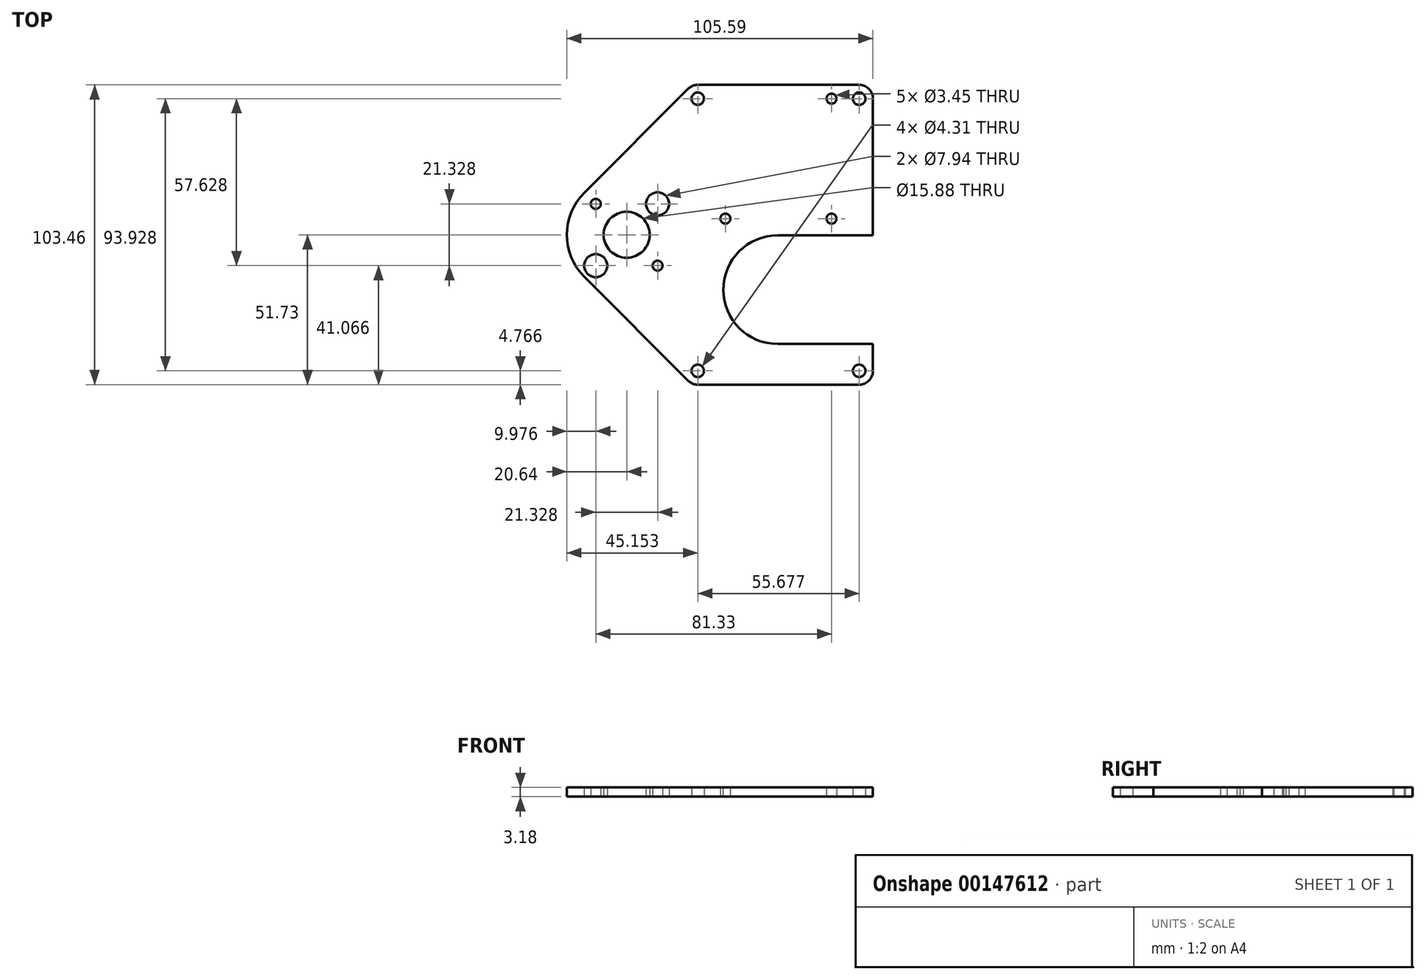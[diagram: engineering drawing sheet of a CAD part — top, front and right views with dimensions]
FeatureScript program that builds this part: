
annotation { "Feature Type Name" : "Feature", "Feature Type Description" : "" }
export const myFeature = defineFeature(function(context is Context, id is Id, definition is map)
    precondition{}
    {
        {
            var Q0;
            Q0=qCreatedBy(makeId("Top.planeOp"),FACE);
            var sketch = newSketch(context, id + "F0", { "sketchPlane" : qUnion([Q0])});
            skPoint(sketch, "E0.rect.middle", {"position": v(0, 0) * mm});
            skCircle(sketch, "E1", {"center": v(0, 0) * mm, "radius": 7.94 * mm});
            skLineSegment(sketch, "E2", {"start": v(0, 0) * mm, "end": v(84.95, 0) * mm, "construction": true});
            skLineSegment(sketch, "E3", {"start": v(84.95, 0) * mm, "end": v(84.95, 0) * mm});
            skLineSegment(sketch, "E4", {"start": v(-14.6, 14.6) * mm, "end": v(21.15, 50.33) * mm});
            skLineSegment(sketch, "E5", {"start": v(-14.6, -14.6) * mm, "end": v(21.15, -50.33) * mm});
            skCircle(sketch, "E6", {"center": v(24.51, 46.96) * mm, "radius": 2.15 * mm});
            skArc(sketch, "E7", {"start": v(24.51, 51.73) * mm, "mid": v(22.7, 51.36) * mm, "end": v(21.15, 50.33) * mm});
            skLineSegment(sketch, "E8", {"start": v(24.51, 51.73) * mm, "end": v(84.95, 51.73) * mm});
            skLineSegment(sketch, "E9", {"start": v(84.95, 51.73) * mm, "end": v(84.95, -51.73) * mm});
            skLineSegment(sketch, "E10", {"start": v(84.95, -51.73) * mm, "end": v(24.51, -51.73) * mm});
            skArc(sketch, "E11", {"start": v(21.15, -50.33) * mm, "mid": v(22.7, -51.36) * mm, "end": v(24.51, -51.73) * mm});
            skLineSegment(sketch, "E12", {"start": v(80.2, 46.96) * mm, "end": v(80.2, 51.73) * mm, "construction": true});
            skLineSegment(sketch, "E13", {"start": v(80.2, 46.96) * mm, "end": v(84.95, 46.96) * mm, "construction": true});
            skLineSegment(sketch, "E14", {"start": v(24.51, 46.96) * mm, "end": v(24.51, 51.73) * mm, "construction": true});
            skCircle(sketch, "E15", {"center": v(80.2, 46.96) * mm, "radius": 2.15 * mm});
            skCircle(sketch, "E16", {"center": v(80.2, -46.96) * mm, "radius": 2.15 * mm});
            skCircle(sketch, "E17", {"center": v(24.51, -46.96) * mm, "radius": 2.15 * mm});
            skArc(sketch, "E18", {"start": v(-14.6, 14.6) * mm, "mid": v(-20.64, 0) * mm, "end": v(-14.6, -14.6) * mm});
            skLineSegment(sketch, "E19", {"start": v(80.2, 46.96) * mm, "end": v(70.67, 46.96) * mm, "construction": true});
            skCircle(sketch, "E20", {"center": v(70.67, 46.96) * mm, "radius": 1.73 * mm});
            skLineSegment(sketch, "E21", {"start": v(24.51, -46.96) * mm, "end": v(80.2, -46.96) * mm, "construction": true});
            skLineSegment(sketch, "E22", {"start": v(70.67, 46.96) * mm, "end": v(70.67, 5.56) * mm, "construction": true});
            skCircle(sketch, "E23", {"center": v(70.67, 5.56) * mm, "radius": 1.73 * mm});
            skLineSegment(sketch, "E24", {"start": v(70.67, 46.96) * mm, "end": v(34.04, 46.96) * mm, "construction": true});
            skLineSegment(sketch, "E25", {"start": v(34.04, 46.96) * mm, "end": v(24.51, 46.96) * mm, "construction": true});
            skLineSegment(sketch, "E26", {"start": v(80.2, 46.96) * mm, "end": v(80.2, -46.96) * mm, "construction": true});
            skLineSegment(sketch, "E27", {"start": v(34.04, 46.96) * mm, "end": v(34.04, 5.56) * mm, "construction": true});
            skCircle(sketch, "E28", {"center": v(34.04, 5.56) * mm, "radius": 1.73 * mm});
            skLineSegment(sketch, "E29.bottom", {"start": v(10.66, -10.66) * mm, "end": v(-10.66, -10.66) * mm, "construction": true});
            skLineSegment(sketch, "E29.top", {"start": v(10.66, 10.66) * mm, "end": v(-10.66, 10.66) * mm, "construction": true});
            skLineSegment(sketch, "E29.left", {"start": v(10.66, -10.66) * mm, "end": v(10.66, 10.66) * mm, "construction": true});
            skLineSegment(sketch, "E29.right", {"start": v(-10.66, -10.66) * mm, "end": v(-10.66, 10.66) * mm, "construction": true});
            skCircle(sketch, "E30", {"center": v(-10.66, 10.66) * mm, "radius": 5.56 * mm, "construction": true});
            skCircle(sketch, "E31", {"center": v(0, 0) * mm, "radius": 9.53 * mm, "construction": true});
            skCircle(sketch, "E32", {"center": v(-10.66, 10.66) * mm, "radius": 1.73 * mm});
            skCircle(sketch, "E33", {"center": v(10.66, 10.66) * mm, "radius": 3.97 * mm});
            skCircle(sketch, "E34", {"center": v(10.66, -10.66) * mm, "radius": 1.73 * mm});
            skCircle(sketch, "E35", {"center": v(-10.66, -10.66) * mm, "radius": 3.97 * mm});
            skSolve(sketch);
        }
        {
            var Q0;
            Q0=qSketchRegion(id+"F0",true);
            extrude(context, id + "F1", {"entities" : qUnion([Q0]), "depth" : 3.17 * mm});
        }
        {
            var Q0;
            Q0=makeQuery(id+"F1.opExtrude","SWEPT_EDGE",EDGE,{"disambiguationData":[OSD([sQuery(id+"F0.wireOp",EDGE,"E8"),sQuery(id+"F0.wireOp",EDGE,"E9")])]});
            var Q1;
            Q1=makeQuery(id+"F1.opExtrude","SWEPT_EDGE",EDGE,{"disambiguationData":[OSD([sQuery(id+"F0.wireOp",EDGE,"E9"),sQuery(id+"F0.wireOp",EDGE,"E10")])]});
            fillet(context, id + "F2", {"entities" : qUnion([Q0, Q1]), "radius" : 4.76 * mm, "tangentPropagation" : true, "allowEdgeOverflow" : false});
        }
        {
            var Q0;
            Q0=makeQuery(id+"F1.opExtrude","CAP_FACE",FACE,{"disambiguationData":[OSD([sQuery(id+"F0.wireOp",EDGE,"E1"),sQuery(id+"F0.wireOp",EDGE,"E4"),sQuery(id+"F0.wireOp",EDGE,"E5"),sQuery(id+"F0.wireOp",EDGE,"E6"),sQuery(id+"F0.wireOp",EDGE,"E7"),sQuery(id+"F0.wireOp",EDGE,"E8"),sQuery(id+"F0.wireOp",EDGE,"E9"),sQuery(id+"F0.wireOp",EDGE,"E10"),sQuery(id+"F0.wireOp",EDGE,"E11"),sQuery(id+"F0.wireOp",EDGE,"c9UVsLf3-3vo0-btpd-LW5h-McrYkxfIfwrX"),sQuery(id+"F0.wireOp",EDGE,"DmsSuh6m-xxGD-tW94-DbP7-TePuitDdWggo"),sQuery(id+"F0.wireOp",EDGE,"E15"),sQuery(id+"F0.wireOp",EDGE,"E16"),sQuery(id+"F0.wireOp",EDGE,"E17"),sQuery(id+"F0.wireOp",EDGE,"DUnib5Ox-MoBG-LOM3-gKAk-fQ2ZFYEBRuNd"),sQuery(id+"F0.wireOp",EDGE,"cTl0YGyF-DTL9-b4bk-yntU-RYKCb7mShI6j"),sQuery(id+"F0.wireOp",EDGE,"E18"),sQuery(id+"F0.wireOp",EDGE,"MRtKpgsU-7xy0-MH5Q-GBLY-cLs65ZSiBn7D"),sQuery(id+"F0.wireOp",EDGE,"3O2D8myY-gLv5-OGMN-T1Rf-2xoa9yZ5CW8g"),sQuery(id+"F0.wireOp",EDGE,"E20"),sQuery(id+"F0.wireOp",EDGE,"q2jaM1ck-fXtA-z5uJ-E1nE-SJ685Pe49XAy"),sQuery(id+"F0.wireOp",EDGE,"E23")])],"isStart":false});
            var sketch = newSketch(context, id + "F3", { "sketchPlane" : qUnion([Q0])});
            skLineSegment(sketch, "E36.bottom", {"start": v(84.95, -37.69) * mm, "end": v(52.07, -37.69) * mm});
            skLineSegment(sketch, "E36.top", {"start": v(84.95, -0.22) * mm, "end": v(52.07, -0.22) * mm});
            skLineSegment(sketch, "E36.left", {"start": v(84.95, -37.69) * mm, "end": v(84.95, -0.22) * mm});
            skLineSegment(sketch, "E36.right", {"start": v(52.07, -37.69) * mm, "end": v(52.07, -0.22) * mm, "construction": true});
            skArc(sketch, "E37", {"start": v(52.07, -0.22) * mm, "mid": v(33.33, -18.95) * mm, "end": v(52.07, -37.69) * mm});
            skSolve(sketch);
        }
        {
            var Q0;
            Q0=qSketchRegion(id+"F3",true);
            var Q1;
            Q1=makeQuery(id+"F1.opExtrude","CAP_FACE",FACE,{"disambiguationData":[OSD([sQuery(id+"F0.wireOp",EDGE,"E1"),sQuery(id+"F0.wireOp",EDGE,"E4"),sQuery(id+"F0.wireOp",EDGE,"E5"),sQuery(id+"F0.wireOp",EDGE,"E6"),sQuery(id+"F0.wireOp",EDGE,"E7"),sQuery(id+"F0.wireOp",EDGE,"E8"),sQuery(id+"F0.wireOp",EDGE,"E9"),sQuery(id+"F0.wireOp",EDGE,"E10"),sQuery(id+"F0.wireOp",EDGE,"E11"),sQuery(id+"F0.wireOp",EDGE,"c9UVsLf3-3vo0-btpd-LW5h-McrYkxfIfwrX"),sQuery(id+"F0.wireOp",EDGE,"DmsSuh6m-xxGD-tW94-DbP7-TePuitDdWggo"),sQuery(id+"F0.wireOp",EDGE,"E15"),sQuery(id+"F0.wireOp",EDGE,"E16"),sQuery(id+"F0.wireOp",EDGE,"E17"),sQuery(id+"F0.wireOp",EDGE,"DUnib5Ox-MoBG-LOM3-gKAk-fQ2ZFYEBRuNd"),sQuery(id+"F0.wireOp",EDGE,"cTl0YGyF-DTL9-b4bk-yntU-RYKCb7mShI6j"),sQuery(id+"F0.wireOp",EDGE,"E18"),sQuery(id+"F0.wireOp",EDGE,"MRtKpgsU-7xy0-MH5Q-GBLY-cLs65ZSiBn7D"),sQuery(id+"F0.wireOp",EDGE,"3O2D8myY-gLv5-OGMN-T1Rf-2xoa9yZ5CW8g"),sQuery(id+"F0.wireOp",EDGE,"E20"),sQuery(id+"F0.wireOp",EDGE,"q2jaM1ck-fXtA-z5uJ-E1nE-SJ685Pe49XAy"),sQuery(id+"F0.wireOp",EDGE,"E23")])],"isStart":true});
            extrude(context, id + "F4", {"entities" : qUnion([Q0]), "operationType" : NewBodyOperationType.REMOVE, "endBound" : BoundingType.UP_TO_SURFACE, "oppositeDirection" : true, "endBoundEntityFace" : qUnion([Q1]), "depth" : 25.4 * mm});
        }
    });
